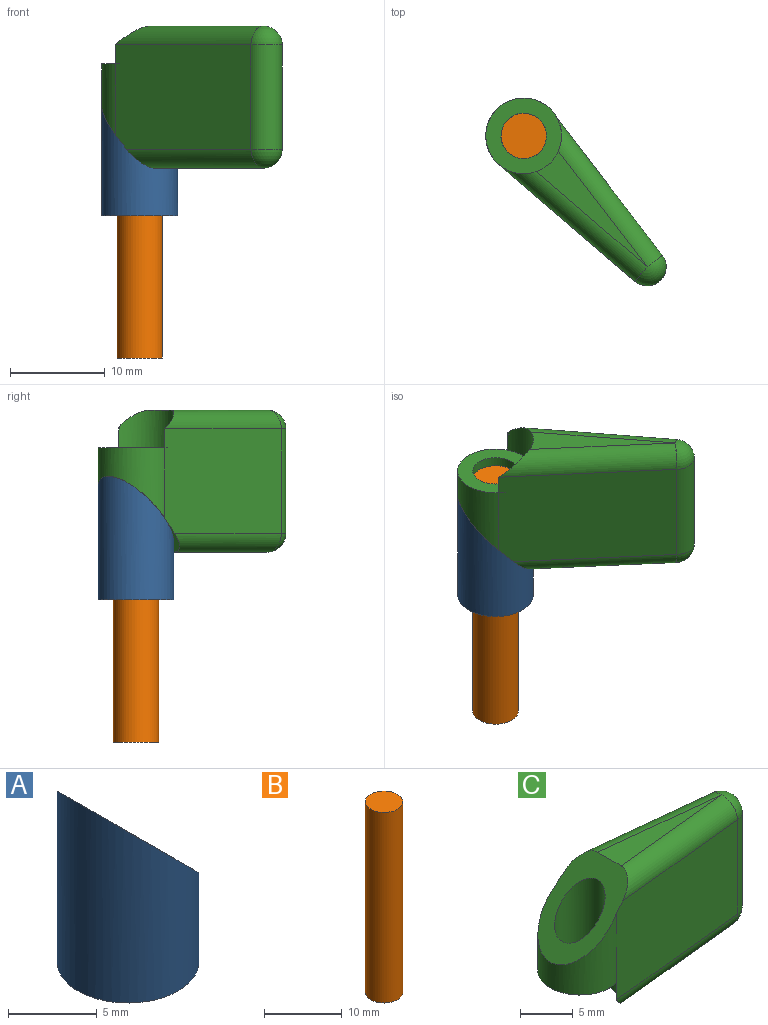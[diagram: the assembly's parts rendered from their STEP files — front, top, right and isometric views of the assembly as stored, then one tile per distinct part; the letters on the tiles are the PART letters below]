
ASSEMBLY  parts=3 mates=2
PART A: 4 faces, bbox 9.7x9.7x14.7 mm
  f0: cylinder r=2.4mm len=11.4mm, axis (0,0,1), area 135.7mm2, adj f2,f3
  f1: cylinder r=4mm len=13mm, axis (0,0,1), area 226.2mm2, adj f2,f3
  f2: plane 8x8mm, normal (0,0,-1), area 32.2mm2, adj f0,f1
  f3: plane 9.68x9.68mm, normal (0.71,0,0.71), area 45.5mm2, adj f0,f1
PART B: 3 faces, bbox 4.8x4.8x30 mm
  f0: cylinder r=2.4mm len=30mm, axis (0,0,-1), area 452.4mm2, adj f1,f2
  f1: plane 4.8x4.8mm, normal (0,0,1), area 18.1mm2, adj f0
  f2: plane 4.8x4.8mm, normal (0,0,-1), area 18.1mm2, adj f0
PART C: 16 faces, bbox 25x8x15 mm
  f0: cylinder r=4mm len=8.13mm, axis (0,0,-1), area 67.6mm2, adj f4,f6,f8,f15
  f1: cylinder r=2mm len=19mm, axis (-0.99,0.11,0), area 53.2mm2, adj f6,f7,f12,f14
  f2: cylinder r=2mm len=18.28mm, axis (0.99,0.1,0), area 52.7mm2, adj f4,f7,f12,f14
  f3: plane 15x3.12mm, normal (0,0,1), area 23.4mm2, adj f8,f9,f11
  f4: plane 18.08x11mm, normal (0.1,-0.99,0), area 199.5mm2, adj f0,f2,f5,f8,f11,f14
  f5: cylinder r=2mm len=11mm, axis (0,0,-1), area 64.6mm2, adj f4,f6,f10,f12
  f6: plane 18.79x11mm, normal (0.11,0.99,0), area 206.6mm2, adj f0,f1,f5,f8,f9,f14
  f7: plane 15.34x3.19mm, normal (0,0,-1), area 23.7mm2, adj f1,f2,f14
  f8: plane 8x8mm, normal (-0.71,0,0.71), area 50.4mm2, adj f0,f3,f4,f6,f9,f11,f13
  f9: cylinder r=2mm len=17.42mm, axis (0.99,-0.11,0), area 50.1mm2, adj f3,f6,f8,f10
  f10: sphere r=2mm, area 11.7mm2, adj f5,f9,f11
  f11: cylinder r=2mm len=17.41mm, axis (-0.99,-0.1,0), area 50.1mm2, adj f3,f4,f8,f10
  f12: sphere r=2mm, area 11.9mm2, adj f1,f2,f5
  f13: cylinder r=2.4mm len=9.43mm, axis (0,0,-1), area 105.6mm2, adj f8,f15
  f14: cylinder r=4mm len=7.82mm, axis (0,0,-1), area 38.7mm2, adj f1,f2,f4,f6,f7,f15
  f15: plane 8x8mm, normal (0,0,-1), area 32.2mm2, adj f0,f13,f14
PLACE A rot(axis=(0,0,-1),46.7deg) t=(-20.64,-0.03,-2.97)mm
PLACE B t=(-20.64,-0.03,-21.01)mm fixed
PLACE C rot(axis=(-0.92,0.4,0),180deg) t=(-20.64,-0.03,14.03)mm
MATE fastened A.f3 <-> C.f8  axis (0.49,-0.51,0.71) through (-20.64,-0.03,3.03)mm
MATE cylindrical B.f0 <-> C.f13  axis (0,0,1) through (-20.64,-0.03,8.99)mm
